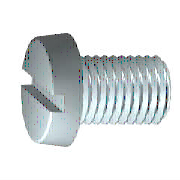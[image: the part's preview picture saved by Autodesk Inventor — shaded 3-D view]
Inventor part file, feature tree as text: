
AUTODESK INVENTOR PART (.ipt)
format: ipt  version: 2017 (Build 210142000, 142)  size: 184,320 bytes
history: native  units: mm (DEFAULTED — no unit token found)
features: sketch x2, extrude x1, plane x1
ambient origin geometry x7: Origin, YZ Plane, XZ Plane, X Axis, Y Axis, Z Axis, Center Point
bodies: Solid1 (feature_tree), Body (feature_tree)
feature tree (4):
  sketch  "Sketch2"  dims[d2=0.429515mm d3=2.6mm d4=4.0mm d5=3.621114mm d8=90.0deg d7=0.0mm d9=7.0mm d10=0.872665mm d11=1.2mm d12=7.0mm d14=0.2mm d15=12.6mm d16=0.0mm d17=0.378885mm d18=0.429515mm d19=1.1mm d20=0.0mm d36=45.0deg d37=0.0mm d39=0.0mm]
  extrude  "Slot"  Depth=12.6mm
  plane  "Work Plane1"
  sketch  "Sketch1"  dims[d0=14.0mm d1=12.6mm]
